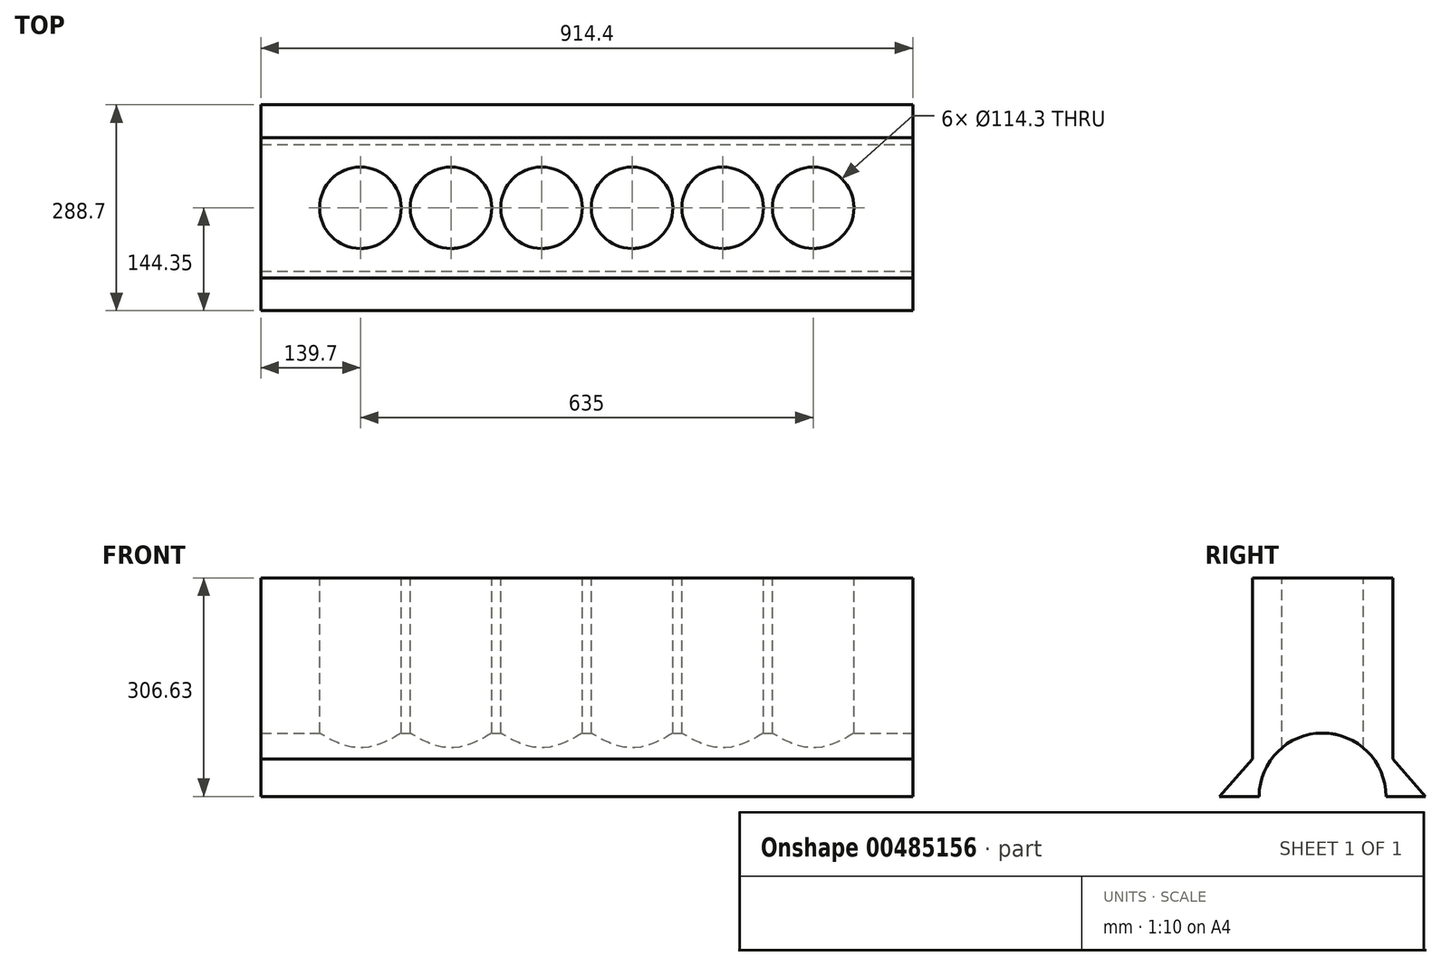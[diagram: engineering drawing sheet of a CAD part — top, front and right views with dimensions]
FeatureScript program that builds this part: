
annotation { "Feature Type Name" : "Feature", "Feature Type Description" : "" }
export const myFeature = defineFeature(function(context is Context, id is Id, definition is map)
    precondition{}
    {
        {
            var Q0;
            Q0=qCreatedBy(makeId("Right.planeOp"),FACE);
            var sketch = newSketch(context, id + "F0", { "sketchPlane" : qUnion([Q0])});
            skLineSegment(sketch, "E0.bottom", {"start": v(98.42, 127) * mm, "end": v(-98.43, 127) * mm});
            skLineSegment(sketch, "E0.top", {"start": v(98.43, -127) * mm, "end": v(-98.42, -127) * mm});
            skLineSegment(sketch, "E0.left", {"start": v(98.42, 127) * mm, "end": v(98.43, -127) * mm});
            skLineSegment(sketch, "E0.right", {"start": v(-98.43, 127) * mm, "end": v(-98.42, -127) * mm});
            skPoint(sketch, "E0.middle", {"position": v(0, 0) * mm});
            skLineSegment(sketch, "E1", {"start": v(-98.42, -127) * mm, "end": v(-144.35, -179.63) * mm});
            skLineSegment(sketch, "E2", {"start": v(98.42, -127) * mm, "end": v(144.35, -179.63) * mm});
            skLineSegment(sketch, "E3", {"start": v(-144.35, -179.63) * mm, "end": v(144.35, -179.63) * mm});
            skSolve(sketch);
        }
        {
            var Q0;
            Q0 = qSketchRegion(id + "F0", true);
            extrude(context, id + "F1", {"entities" : qUnion([Q0]), "oppositeDirection" : true, "depth" : 914.4 * mm});
        }
        {
            var Q0;
            Q0=makeQuery(id+"F1.opExtrude","SWEPT_FACE",FACE,{"disambiguationData":[OSD([sQuery(id+"F0.wireOp",EDGE,"E0.bottom")])]});
            var sketch = newSketch(context, id + "F2", { "sketchPlane" : qUnion([Q0])});
            skLineSegment(sketch, "E4", {"start": v(-914.4, 0) * mm, "end": v(0, 0) * mm, "construction": true});
            skPoint(sketch, "E5", {"position": v(-647.7, 0) * mm});
            skPoint(sketch, "E6", {"position": v(-520.7, 0) * mm});
            skPoint(sketch, "E7", {"position": v(-393.7, 0) * mm});
            skPoint(sketch, "E8", {"position": v(-266.7, 0) * mm});
            skPoint(sketch, "E9", {"position": v(-139.7, 0) * mm});
            skPoint(sketch, "E10", {"position": v(-774.7, 0) * mm});
            skSolve(sketch);
        }
        {
            var Q0;
            Q0=sQuery(id+"F2.wireOp",VERTEX,"E10");
            var Q1;
            Q1=sQuery(id+"F2.wireOp",VERTEX,"E5");
            var Q2;
            Q2=sQuery(id+"F2.wireOp",VERTEX,"E6");
            var Q3;
            Q3=sQuery(id+"F2.wireOp",VERTEX,"E7");
            var Q4;
            Q4=sQuery(id+"F2.wireOp",VERTEX,"E8");
            var Q5;
            Q5=sQuery(id+"F2.wireOp",VERTEX,"E9");
            var Q6;
            Q6=makeQuery(id+"F1.opExtrude","SWEPT_BODY",BODY,{"disambiguationData":[OSD([sQuery(id+"F0.wireOp",EDGE,"E0.bottom"),sQuery(id+"F0.wireOp",EDGE,"E0.left"),sQuery(id+"F0.wireOp",EDGE,"E0.right"),sQuery(id+"F0.wireOp",EDGE,"E1"),sQuery(id+"F0.wireOp",EDGE,"E2"),sQuery(id+"F0.wireOp",EDGE,"E3")])]});
            hole(context, id + "F3", {"style" : HoleStyle.SIMPLE, "endStyle" : HoleEndStyle.THROUGH, "holeDiameter" : 114.3 * mm, "isTappedThrough" : true, "tappedDepth" : 12.7 * mm, "tapClearance" : 3, "locations" : qUnion([Q0, Q1, Q2, Q3, Q4, Q5]), "scope" : qUnion([Q6])});
        }
        {
            var Q0;
            Q0=makeQuery(id+"F1.opExtrude","CAP_FACE",FACE,{"disambiguationData":[OSD([sQuery(id+"F0.wireOp",EDGE,"E0.bottom"),sQuery(id+"F0.wireOp",EDGE,"E0.left"),sQuery(id+"F0.wireOp",EDGE,"E0.right"),sQuery(id+"F0.wireOp",EDGE,"E1"),sQuery(id+"F0.wireOp",EDGE,"E2"),sQuery(id+"F0.wireOp",EDGE,"E3")])],"isStart":true});
            var sketch = newSketch(context, id + "F4", { "sketchPlane" : qUnion([Q0])});
            skCircle(sketch, "E11", {"center": v(0, -179.63) * mm, "radius": 88.9 * mm});
            skSolve(sketch);
        }
        {
            var Q0;
            {var subQ0=sQuery(id+"F4.wireOp",EDGE,"E11");var subQ1=makeQuery(id+"F1.opExtrude","CAP_EDGE",EDGE,{"disambiguationData":[OSD([sQuery(id+"F0.wireOp",EDGE,"E3")])],"isStart":true});var subQ2=makeQuery(id+"F4.imprint","INTERSECT",VERTEX,{"disambiguationData":[OD(0.0)],"derivedFrom":[subQ1,subQ0]});Q0=makeQuery(id+"F4.imprint","IMPRINT",FACE,{"disambiguationData":[TD([[makeQuery(id+"F4.imprint","IMPRINT",EDGE,{"disambiguationData":[TD([[subQ2,1.0]])],"derivedFrom":subQ0}),1.0]])]});}
            extrude(context, id + "F5", {"entities" : qUnion([Q0]), "operationType" : NewBodyOperationType.REMOVE, "oppositeDirection" : true, "depth" : 914.4 * mm});
        }
    });
